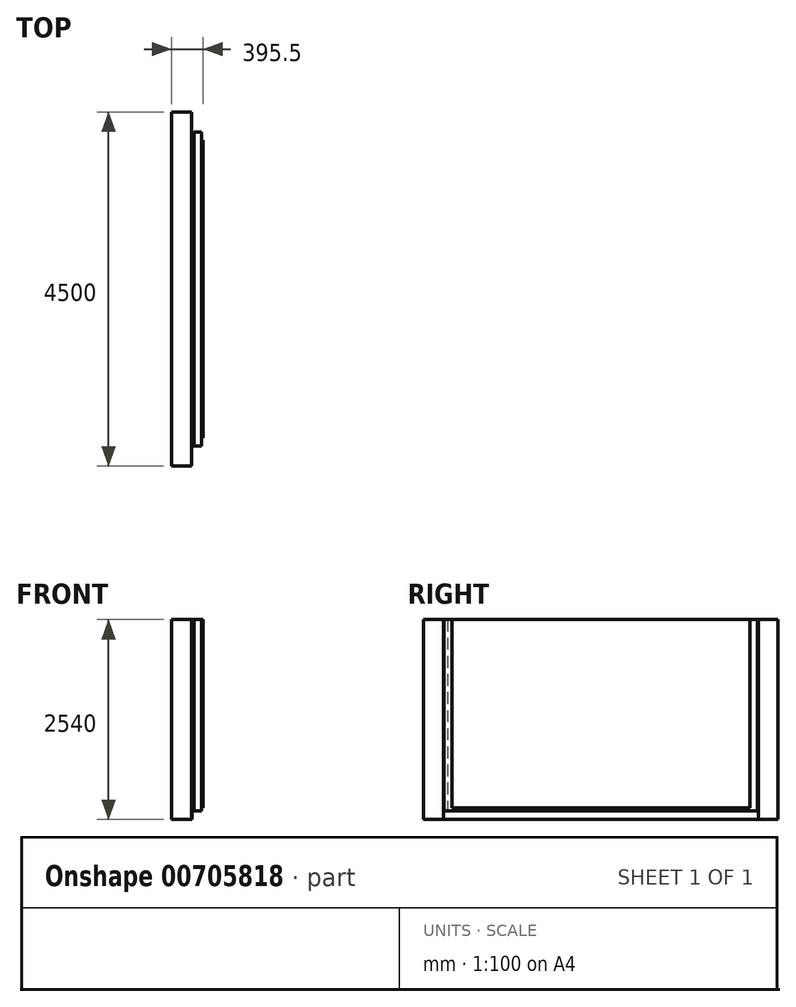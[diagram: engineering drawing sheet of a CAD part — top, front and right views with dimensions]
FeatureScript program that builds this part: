
annotation { "Feature Type Name" : "Feature", "Feature Type Description" : "" }
export const myFeature = defineFeature(function(context is Context, id is Id, definition is map)
    precondition{}
    {
        {
            var Q0;
            Q0=qCreatedBy(makeId("Top.planeOp"),FACE);
            var sketch = newSketch(context, id + "F0", { "sketchPlane" : qUnion([Q0])});
            skLineSegment(sketch, "E0.bottom", {"start": v(-18.66, -55.84) * mm, "end": v(231.34, -55.84) * mm});
            skLineSegment(sketch, "E0.top", {"start": v(-18.66, 4444.16) * mm, "end": v(231.34, 4444.16) * mm});
            skLineSegment(sketch, "E0.left", {"start": v(-18.66, -55.84) * mm, "end": v(-18.66, 4444.16) * mm});
            skLineSegment(sketch, "E0.right", {"start": v(231.34, -55.84) * mm, "end": v(231.34, 4444.16) * mm});
            skSolve(sketch);
        }
        {
            var Q0;
            Q0=makeQuery(id+"F0.imprint","IMPRINT",FACE,{"disambiguationData":[TD([[makeQuery(id+"F0.imprint","IMPRINT",EDGE,{"derivedFrom":sQuery(id+"F0.wireOp",EDGE,"E0.bottom")}),1.0]])]});
            extrude(context, id + "F1", {"entities" : qUnion([Q0]), "depth" : 2540 * mm, "offsetDistance" : 25 * mm});
        }
        {
            var Q0;
            Q0=makeQuery(id+"F1.opExtrude","SWEPT_FACE",FACE,{"disambiguationData":[OSD([sQuery(id+"F0.wireOp",EDGE,"E0.right")])]});
            var sketch = newSketch(context, id + "F2", { "sketchPlane" : qUnion([Q0])});
            skLineSegment(sketch, "E1.bottom", {"start": v(194.16, 2540) * mm, "end": v(4194.16, 2540) * mm});
            skLineSegment(sketch, "E1.top", {"start": v(194.16, 0) * mm, "end": v(4194.16, 0) * mm});
            skLineSegment(sketch, "E1.left", {"start": v(194.16, 2540) * mm, "end": v(194.16, 0) * mm});
            skLineSegment(sketch, "E1.right", {"start": v(4194.16, 2540) * mm, "end": v(4194.16, 0) * mm});
            skSolve(sketch);
        }
        {
            var Q0;
            Q0=makeQuery(id+"F2.imprint","IMPRINT",FACE,{"disambiguationData":[TD([[makeQuery(id+"F2.imprint","IMPRINT",EDGE,{"derivedFrom":sQuery(id+"F2.wireOp",EDGE,"E1.bottom")}),-1.0]])]});
            extrude(context, id + "F3", {"entities" : qUnion([Q0]), "depth" : 8 * mm, "offsetDistance" : 25 * mm});
        }
        {
            var Q0;
            Q0=makeQuery(id+"F3.opExtrude","CAP_FACE",FACE,{"disambiguationData":[OSD([sQuery(id+"F2.wireOp",EDGE,"E1.bottom"),sQuery(id+"F2.wireOp",EDGE,"E1.top"),sQuery(id+"F2.wireOp",EDGE,"E1.left"),sQuery(id+"F2.wireOp",EDGE,"E1.right")])],"isStart":false});
            var sketch = newSketch(context, id + "F4", { "sketchPlane" : qUnion([Q0])});
            skLineSegment(sketch, "E2.bottom", {"start": v(202.16, 2540) * mm, "end": v(249.16, 2540) * mm});
            skLineSegment(sketch, "E2.top", {"start": v(202.16, 108) * mm, "end": v(249.16, 108) * mm});
            skLineSegment(sketch, "E2.left", {"start": v(202.16, 2540) * mm, "end": v(202.16, 108) * mm});
            skLineSegment(sketch, "E2.right", {"start": v(249.16, 2540) * mm, "end": v(249.16, 108) * mm});
            skSolve(sketch);
        }
        {
            var Q0;
            Q0=makeQuery(id+"F4.imprint","IMPRINT",FACE,{"disambiguationData":[TD([[makeQuery(id+"F4.imprint","IMPRINT",EDGE,{"derivedFrom":sQuery(id+"F4.wireOp",EDGE,"E2.bottom")}),-1.0]])]});
            extrude(context, id + "F5", {"entities" : qUnion([Q0]), "depth" : 25 * mm, "offsetDistance" : 25 * mm});
        }
        {
            var Q0;
            Q0=makeQuery(id+"F5.opExtrude","CAP_FACE",FACE,{"disambiguationData":[OSD([sQuery(id+"F4.wireOp",EDGE,"E2.bottom"),sQuery(id+"F4.wireOp",EDGE,"E2.top"),sQuery(id+"F4.wireOp",EDGE,"E2.left"),sQuery(id+"F4.wireOp",EDGE,"E2.right")])],"isStart":false});
            var sketch = newSketch(context, id + "F6", { "sketchPlane" : qUnion([Q0])});
            skLineSegment(sketch, "E3.bottom", {"start": v(202.16, 2540) * mm, "end": v(4186.16, 2540) * mm});
            skLineSegment(sketch, "E3.top", {"start": v(202.16, 108) * mm, "end": v(4186.16, 108) * mm});
            skLineSegment(sketch, "E3.left", {"start": v(202.16, 2540) * mm, "end": v(202.16, 108) * mm});
            skLineSegment(sketch, "E3.right", {"start": v(4186.16, 2540) * mm, "end": v(4186.16, 108) * mm});
            skSolve(sketch);
        }
        {
            var Q0;
            {var subQ0=sQuery(id+"F6.wireOp",EDGE,"E3.left");Q0=makeQuery(id+"F6.imprint","IMPRINT",FACE,{"disambiguationData":[TD([[makeQuery(id+"F6.imprint","IMPRINT",EDGE,{"derivedFrom":subQ0}),1.0]])]});}
            var Q1;
            {var subQ2=sQuery(id+"F6.wireOp",EDGE,"E3.right");Q1=makeQuery(id+"F6.imprint","IMPRINT",FACE,{"disambiguationData":[TD([[makeQuery(id+"F6.imprint","IMPRINT",EDGE,{"derivedFrom":subQ2}),-1.0]])]});}
            extrude(context, id + "F7", {"entities" : qUnion([Q0, Q1]), "depth" : 100 * mm, "offsetDistance" : 25 * mm});
        }
        {
            var Q0;
            Q0=makeQuery(id+"F7.opExtrude","CAP_FACE",FACE,{"disambiguationData":[OSD([sQuery(id+"F6.wireOp",EDGE,"E3.bottom"),sQuery(id+"F6.wireOp",EDGE,"E3.top"),sQuery(id+"F6.wireOp",EDGE,"E3.left"),sQuery(id+"F6.wireOp",EDGE,"E3.right")])],"isStart":false});
            var sketch = newSketch(context, id + "F8", { "sketchPlane" : qUnion([Q0])});
            skLineSegment(sketch, "E4.bottom", {"start": v(302.16, 2540) * mm, "end": v(4086.16, 2540) * mm});
            skLineSegment(sketch, "E4.top", {"start": v(302.16, 148) * mm, "end": v(4086.16, 148) * mm});
            skLineSegment(sketch, "E4.left", {"start": v(302.16, 2540) * mm, "end": v(302.16, 148) * mm});
            skLineSegment(sketch, "E4.right", {"start": v(4086.16, 2540) * mm, "end": v(4086.16, 148) * mm});
            skSolve(sketch);
        }
        {
            var Q0;
            Q0=makeQuery(id+"F8.imprint","IMPRINT",FACE,{"disambiguationData":[TD([[makeQuery(id+"F8.imprint","IMPRINT",EDGE,{"derivedFrom":sQuery(id+"F8.wireOp",EDGE,"E4.bottom")}),-1.0]])]});
            extrude(context, id + "F9", {"entities" : qUnion([Q0]), "depth" : 12.5 * mm, "offsetDistance" : 25 * mm});
        }
    });
